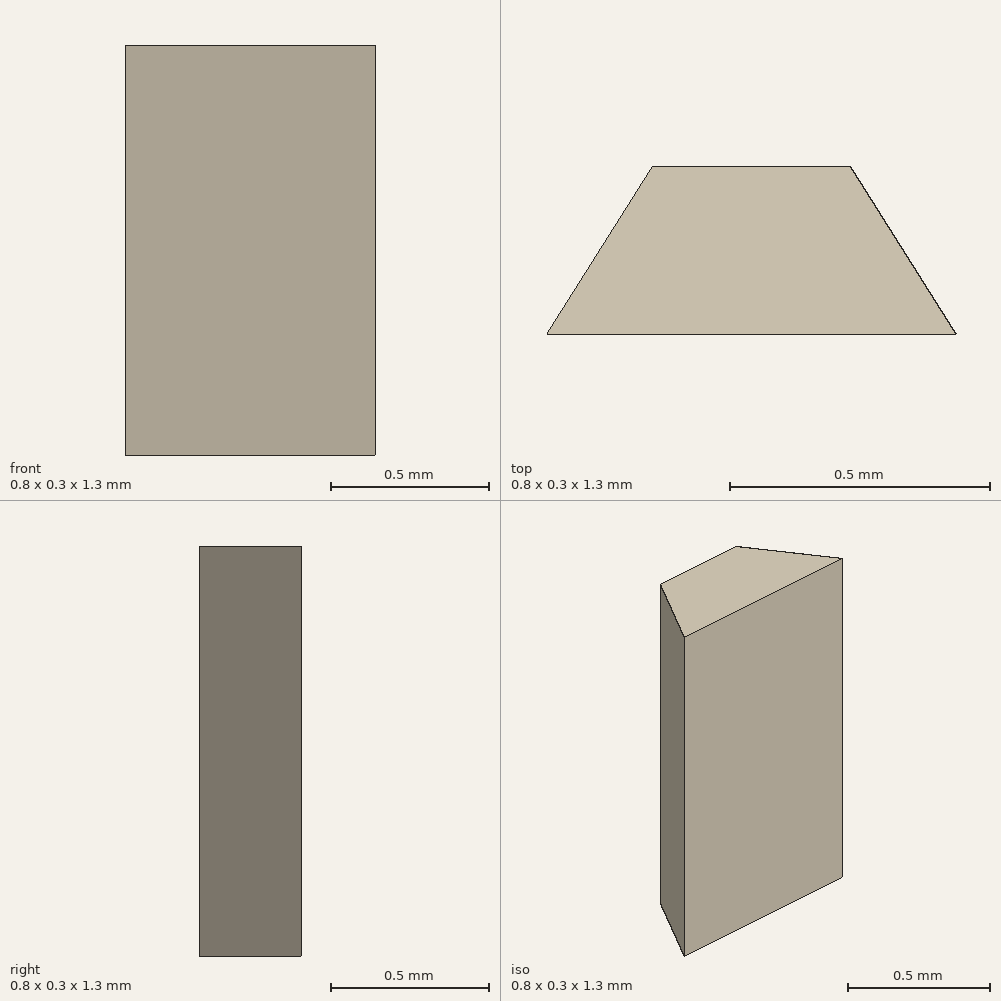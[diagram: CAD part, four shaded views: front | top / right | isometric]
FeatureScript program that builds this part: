
annotation { "Feature Type Name" : "Feature", "Feature Type Description" : "" }
export const myFeature = defineFeature(function(context is Context, id is Id, definition is map)
    precondition{}
    {
        {
            var Q0;
            Q0=qCreatedBy(makeId("Top.planeOp"),FACE);
            var sketch = newSketch(context, id + "F0", { "sketchPlane" : qUnion([Q0])});
            skLineSegment(sketch, "E0.top", {"start": v(0, 0.33) * mm, "end": v(0.38, 0.33) * mm});
            skLineSegment(sketch, "E1", {"start": v(0.58, 0) * mm, "end": v(0.38, 0.33) * mm});
            skLineSegment(sketch, "E2", {"start": v(0, 0.33) * mm, "end": v(-0.2, 0) * mm});
            skLineSegment(sketch, "E3", {"start": v(-0.2, 0) * mm, "end": v(0.58, 0) * mm});
            skSolve(sketch);
        }
        {
            var Q0;
            Q0=makeQuery(id+"F0.imprint","IMPRINT",FACE,{"disambiguationData":[TD([[makeQuery(id+"F0.imprint","IMPRINT",EDGE,{"derivedFrom":sQuery(id+"F0.wireOp",EDGE,"E0.top")}),-1.0]])]});
            extrude(context, id + "F1", {"entities" : qUnion([Q0]), "depth" : 1.3 * mm});
        }
    });
